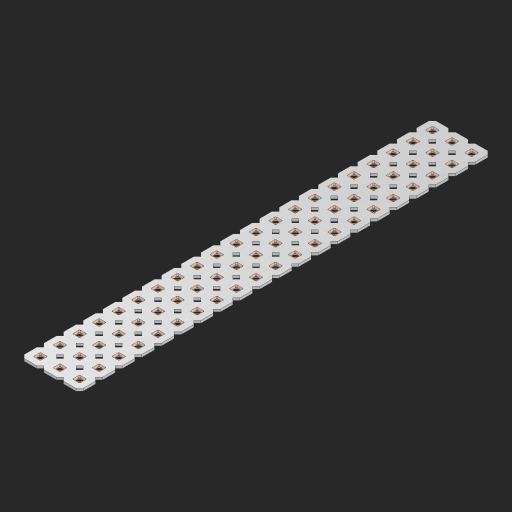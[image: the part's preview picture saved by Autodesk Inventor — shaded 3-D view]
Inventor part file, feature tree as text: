
AUTODESK INVENTOR PART (.ipt)
format: ipt  version: 2023 (Build 270158000, 158)  size: 1,005,056 bytes
history: native  units: in
note: dims shown in document units (in); Inventor stores cm internally (conversion verified against a paired STEP export)
features: other x64, extrude x62, sketch x2, pattern_linear x1
ambient origin geometry x8: Origin, YZ Plane, XZ Plane, XY Plane, X Axis, Y Axis, Z Axis, Center Point
bodies: Solid1 (feature_tree), Body (feature_tree)
feature tree (129):
  pattern_linear  "Rectangular Pattern1"  Spacing1=0.09in  [1 undecoded]
  sketch  "Sketch1"  dims[d1=0.5in]
  sketch  "Sketch2"  dims[d2=0.182in d3=0.09in d4=0.09in d5=0.09in d6=0.09in d7=0.09in d8=0.09in d9=0.09in d10=0.09in d11=0.02in d13=0.0in d14=0.172in d15=0.0625in d16=0.0in d19=0.5in d22=0.5in]
  other  "Srf1"
  other  "Srf126"
  other  "Srf127"
  other  "Srf128"
  other  "Srf129"
  other  "Srf130"
  other  "Srf131"
  other  "Srf250"
  other  "Srf251"
  other  "Srf252"
  other  "Srf253"
  other  "Srf254"
  other  "Srf255"
  other  "Srf256"
  other  "Srf257"
  other  "Srf258"
  other  "Srf259"
  other  "Srf260"
  other  "Srf261"
  other  "Srf262"
  other  "Srf263"
  other  "Srf268"
  other  "Srf269"
  other  "Srf270"
  other  "Srf271"
  other  "Srf272"
  other  "Srf273"
  other  "Srf274"
  other  "Srf275"
  other  "Srf276"
  other  "Srf277"
  other  "Srf278"
  other  "Srf279"
  other  "Srf280"
  other  "Srf281"
  other  "Srf282"
  other  "Srf283"
  other  "Srf284"
  other  "Srf285"
  other  "Srf286"
  other  "Srf287"
  other  "Srf288"
  other  "Srf293"
  other  "Srf294"
  other  "Srf295"
  other  "Srf296"
  other  "Srf297"
  other  "Srf298"
  other  "Srf299"
  other  "Srf300"
  other  "Srf301"
  other  "Srf302"
  other  "Srf303"
  other  "Srf304"
  other  "Srf305"
  other  "Srf306"
  other  "Srf307"
  other  "Srf308"
  other  "Srf309"
  other  "Srf310"
  other  "Srf311"
  other  "Srf312"
  other  "Srf313"
  other  "Circle"
  extrude  "ExtrusionSrf126"  Depth=0.09in
  extrude  "ExtrusionSrf127"  Depth=0.09in
  extrude  "ExtrusionSrf128"  Depth=0.09in
  extrude  "ExtrusionSrf129"  Depth=0.09in
  extrude  "ExtrusionSrf130"  Depth=0.09in
  extrude  "ExtrusionSrf131"  Depth=0.09in
  extrude  "ExtrusionSrf250"  Depth=0.09in
  extrude  "ExtrusionSrf251"  Depth=0.02in
  extrude  "ExtrusionSrf252"  TaperAngle=0.0deg  [1 undecoded]
  extrude  "ExtrusionSrf253"  Depth=0.5in
  extrude  "ExtrusionSrf254"  Depth=0.0625in TaperAngle=0.0deg
  extrude  "ExtrusionSrf255"  Depth=0.5in
  extrude  "ExtrusionSrf256"  Depth=0.5in
  extrude  "ExtrusionSrf257"  [1 undecoded]
  extrude  "ExtrusionSrf258"  [1 undecoded]
  extrude  "ExtrusionSrf259"  [1 undecoded]
  extrude  "ExtrusionSrf260"  [1 undecoded]
  extrude  "ExtrusionSrf261"  [1 undecoded]
  extrude  "ExtrusionSrf262"  [1 undecoded]
  extrude  "ExtrusionSrf263"  [1 undecoded]
  extrude  "ExtrusionSrf268"  [1 undecoded]
  extrude  "ExtrusionSrf269"  [1 undecoded]
  extrude  "ExtrusionSrf270"  [1 undecoded]
  extrude  "ExtrusionSrf271"  [1 undecoded]
  extrude  "ExtrusionSrf272"  [1 undecoded]
  extrude  "ExtrusionSrf273"  [1 undecoded]
  extrude  "ExtrusionSrf274"  [1 undecoded]
  extrude  "ExtrusionSrf275"  [1 undecoded]
  extrude  "ExtrusionSrf276"  [1 undecoded]
  extrude  "ExtrusionSrf277"  [1 undecoded]
  extrude  "ExtrusionSrf278"  [1 undecoded]
  extrude  "ExtrusionSrf279"  [1 undecoded]
  extrude  "ExtrusionSrf280"  [1 undecoded]
  extrude  "ExtrusionSrf281"  [1 undecoded]
  extrude  "ExtrusionSrf282"  [1 undecoded]
  extrude  "ExtrusionSrf283"  [1 undecoded]
  extrude  "ExtrusionSrf284"  [1 undecoded]
  extrude  "ExtrusionSrf285"  [1 undecoded]
  extrude  "ExtrusionSrf286"  [1 undecoded]
  extrude  "ExtrusionSrf287"  [1 undecoded]
  extrude  "ExtrusionSrf288"  [1 undecoded]
  extrude  "ExtrusionSrf293"  [1 undecoded]
  extrude  "ExtrusionSrf294"  [1 undecoded]
  extrude  "ExtrusionSrf295"  [1 undecoded]
  extrude  "ExtrusionSrf296"  [1 undecoded]
  extrude  "ExtrusionSrf297"  [1 undecoded]
  extrude  "ExtrusionSrf298"  [1 undecoded]
  extrude  "ExtrusionSrf299"  [1 undecoded]
  extrude  "ExtrusionSrf300"  [1 undecoded]
  extrude  "ExtrusionSrf301"  [1 undecoded]
  extrude  "ExtrusionSrf302"  [1 undecoded]
  extrude  "ExtrusionSrf303"  [1 undecoded]
  extrude  "ExtrusionSrf304"  [1 undecoded]
  extrude  "ExtrusionSrf305"  [1 undecoded]
  extrude  "ExtrusionSrf306"  [1 undecoded]
  extrude  "ExtrusionSrf307"  [1 undecoded]
  extrude  "ExtrusionSrf308"  [1 undecoded]
  extrude  "ExtrusionSrf309"  [1 undecoded]
  extrude  "ExtrusionSrf310"  [1 undecoded]
  extrude  "ExtrusionSrf311"  [1 undecoded]
  extrude  "ExtrusionSrf312"  [1 undecoded]
  extrude  "ExtrusionSrf313"  [1 undecoded]
note: 51 required parameter values undecoded (feature->parameter linkage not recoverable at this tier; creation-order binding heuristic only, values carry confidence <= 0.55)
